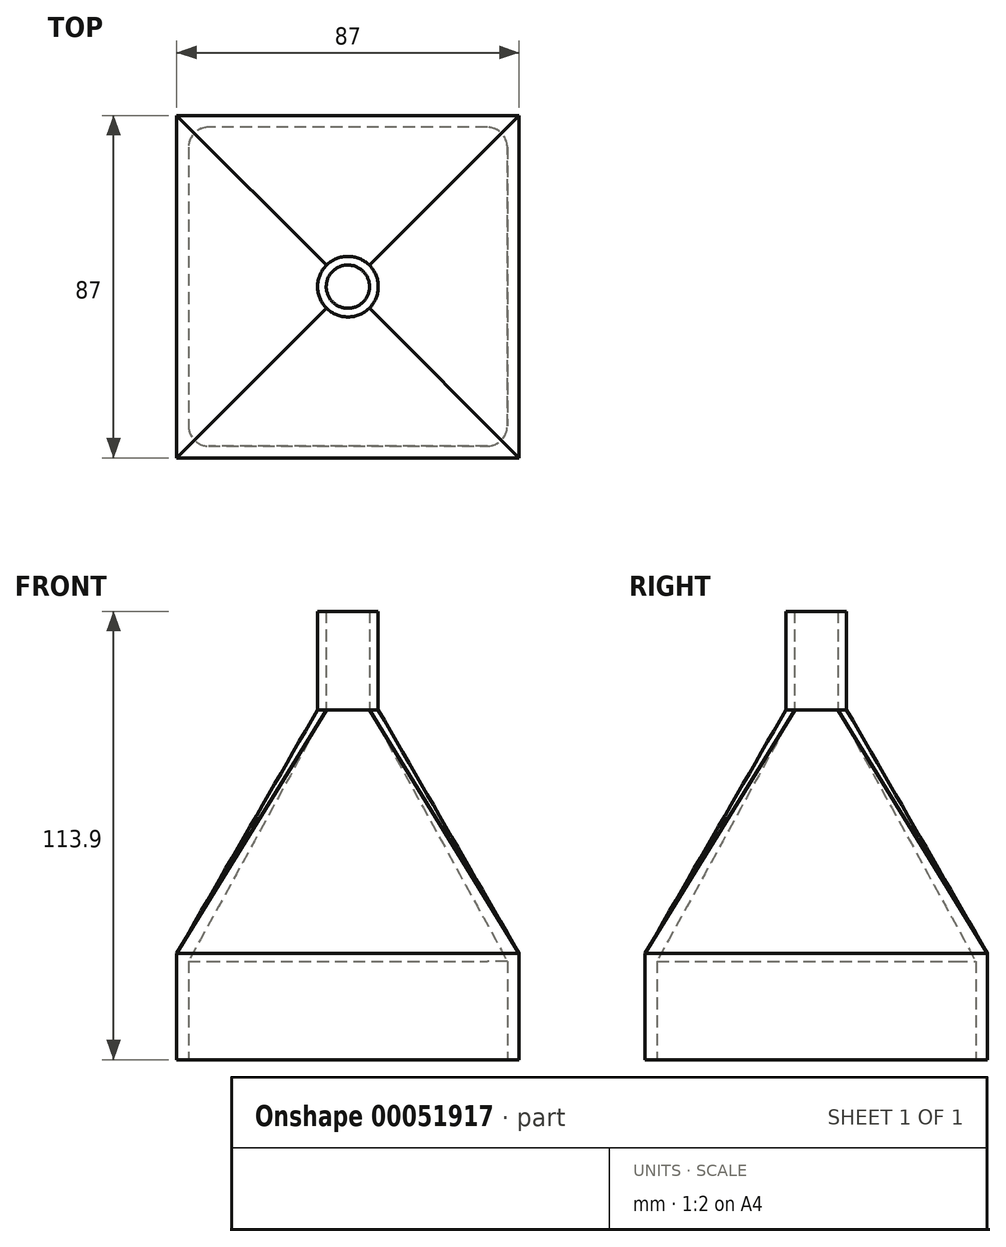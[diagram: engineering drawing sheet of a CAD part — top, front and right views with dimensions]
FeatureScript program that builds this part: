
annotation { "Feature Type Name" : "Feature", "Feature Type Description" : "" }
export const myFeature = defineFeature(function(context is Context, id is Id, definition is map)
    precondition{}
    {
        {
            var Q0;
            Q0=qCreatedBy(makeId("Top.planeOp"),FACE);
            var sketch = newSketch(context, id + "F0", { "sketchPlane" : qUnion([Q0])});
            skLineSegment(sketch, "E0.rect.bottom", {"start": v(35.42, 40.5) * mm, "end": v(-35.42, 40.5) * mm});
            skLineSegment(sketch, "E0.rect.top", {"start": v(35.42, -40.5) * mm, "end": v(-35.42, -40.5) * mm});
            skLineSegment(sketch, "E0.rect.left", {"start": v(40.5, 35.42) * mm, "end": v(40.5, -35.42) * mm});
            skLineSegment(sketch, "E0.rect.right", {"start": v(-40.5, 35.42) * mm, "end": v(-40.5, -35.42) * mm});
            skPoint(sketch, "E0.rect.middle", {"position": v(0, 0) * mm});
            skPoint(sketch, "E1.visualSharp", {"position": v(-40.5, 40.5) * mm});
            skArc(sketch, "E1.filletArc", {"start": v(-35.42, 40.5) * mm, "mid": v(-39, 39) * mm, "end": v(-40.5, 35.42) * mm});
            skPoint(sketch, "E2.visualSharp", {"position": v(40.5, 40.5) * mm});
            skArc(sketch, "E2.filletArc", {"start": v(40.5, 35.42) * mm, "mid": v(39, 39) * mm, "end": v(35.42, 40.5) * mm});
            skPoint(sketch, "E3.visualSharp", {"position": v(40.5, -40.5) * mm});
            skArc(sketch, "E3.filletArc", {"start": v(35.42, -40.5) * mm, "mid": v(39, -39) * mm, "end": v(40.5, -35.42) * mm});
            skPoint(sketch, "E4.visualSharp", {"position": v(-40.5, -40.5) * mm});
            skArc(sketch, "E4.filletArc", {"start": v(-40.5, -35.42) * mm, "mid": v(-39, -39) * mm, "end": v(-35.42, -40.5) * mm});
            skLineSegment(sketch, "E5.rect.bottom", {"start": v(43.5, 43.5) * mm, "end": v(-43.5, 43.5) * mm});
            skLineSegment(sketch, "E5.rect.top", {"start": v(43.5, -43.5) * mm, "end": v(-43.5, -43.5) * mm});
            skLineSegment(sketch, "E5.rect.left", {"start": v(43.5, 43.5) * mm, "end": v(43.5, -43.5) * mm});
            skLineSegment(sketch, "E5.rect.right", {"start": v(-43.5, 43.5) * mm, "end": v(-43.5, -43.5) * mm});
            skSolve(sketch);
        }
        {
            var Q0;
            Q0=makeQuery(id+"F0.imprint","IMPRINT",FACE,{"disambiguationData":[TD([[makeQuery(id+"F0.imprint","IMPRINT",EDGE,{"derivedFrom":sQuery(id+"F0.wireOp",EDGE,"E0.rect.bottom")}),-1.0]])]});
            extrude(context, id + "F1", {"entities" : qUnion([Q0]), "depth" : 25 * mm});
        }
        {
            var Q0;
            Q0=qCreatedBy(makeId("Top.planeOp"),FACE);
            cPlane(context, id + "F2", {"entities" : qUnion([Q0]), "cplaneType" : CPlaneType.OFFSET, "offset" : 88.9 * mm, "width" : 150 * mm, "height" : 150 * mm});
        }
        {
            var Q0;
            Q0=qCreatedBy(id+"F2.planeOp",FACE);
            var sketch = newSketch(context, id + "F3", { "sketchPlane" : qUnion([Q0])});
            skCircle(sketch, "E6", {"center": v(0, 0) * mm, "radius": 7.7 * mm});
            skSolve(sketch);
        }
        {
            var Q0;
            Q0=makeQuery(id+"F1.opExtrude","CAP_FACE",FACE,{"disambiguationData":[OSD([sQuery(id+"F0.wireOp",EDGE,"E0.rect.bottom"),sQuery(id+"F0.wireOp",EDGE,"E0.rect.top"),sQuery(id+"F0.wireOp",EDGE,"E0.rect.left"),sQuery(id+"F0.wireOp",EDGE,"E0.rect.right"),sQuery(id+"F0.wireOp",EDGE,"E1.filletArc"),sQuery(id+"F0.wireOp",EDGE,"E2.filletArc"),sQuery(id+"F0.wireOp",EDGE,"E3.filletArc"),sQuery(id+"F0.wireOp",EDGE,"E4.filletArc"),sQuery(id+"F0.wireOp",EDGE,"E5.rect.bottom"),sQuery(id+"F0.wireOp",EDGE,"E5.rect.top"),sQuery(id+"F0.wireOp",EDGE,"E5.rect.left"),sQuery(id+"F0.wireOp",EDGE,"E5.rect.right")])],"isStart":false});
            var sketch = newSketch(context, id + "F4", { "sketchPlane" : qUnion([Q0])});
            skLineSegment(sketch, "E7.rect.bottom", {"start": v(43.5, 43.5) * mm, "end": v(-43.5, 43.5) * mm});
            skLineSegment(sketch, "E7.rect.top", {"start": v(43.5, -43.5) * mm, "end": v(-43.5, -43.5) * mm});
            skLineSegment(sketch, "E7.rect.left", {"start": v(43.5, 43.5) * mm, "end": v(43.5, -43.5) * mm});
            skLineSegment(sketch, "E7.rect.right", {"start": v(-43.5, 43.5) * mm, "end": v(-43.5, -43.5) * mm});
            skPoint(sketch, "E7.rect.middle", {"position": v(0, 0) * mm});
            skSolve(sketch);
        }
        {
            var Q0;
            Q0=qSketchRegion(id+"F4",true);
            extrude(context, id + "F5", {"entities" : qUnion([Q0]), "operationType" : NewBodyOperationType.ADD, "depth" : 2 * mm});
        }
        {
            var Q1;
            Q1=makeQuery(id+"F5.opExtrude","CAP_FACE",FACE,{"disambiguationData":[OSD([sQuery(id+"F4.wireOp",EDGE,"E7.rect.bottom"),sQuery(id+"F4.wireOp",EDGE,"E7.rect.top"),sQuery(id+"F4.wireOp",EDGE,"E7.rect.left"),sQuery(id+"F4.wireOp",EDGE,"E7.rect.right")])],"isStart":false});
            var Q2;
            Q2=makeQuery(id+"F3.imprint","IMPRINT",FACE,{"disambiguationData":[TD([[makeQuery(id+"F3.imprint","IMPRINT",EDGE,{"derivedFrom":sQuery(id+"F3.wireOp",EDGE,"E6")}),1.0]])]});
            loft(context, id + "F6", {"operationType" : NewBodyOperationType.ADD, "sheetProfilesArray" : [{ "sheetProfileEntities" : qUnion([Q1]) }, { "sheetProfileEntities" : qUnion([Q2]) }]});
        }
        {
            var Q0;
            Q0=makeQuery(id+"F6.opLoft","CAP_FACE",FACE,{"disambiguationData":[OSD([makeQuery(id+"F3.imprint","IMPRINT",FACE,{"disambiguationData":[TD([[makeQuery(id+"F3.imprint","IMPRINT",EDGE,{"derivedFrom":sQuery(id+"F3.wireOp",EDGE,"E6")}),1.0]])]})])],"isStart":true});
            var sketch = newSketch(context, id + "F7", { "sketchPlane" : qUnion([Q0])});
            skCircle(sketch, "E8", {"center": v(0, 0) * mm, "radius": 5.5 * mm});
            skSolve(sketch);
        }
        {
            var Q1;
            Q1=makeQuery(id+"F5.opExtrude","CAP_FACE",FACE,{"disambiguationData":[OSD([sQuery(id+"F4.wireOp",EDGE,"E7.rect.bottom"),sQuery(id+"F4.wireOp",EDGE,"E7.rect.top"),sQuery(id+"F4.wireOp",EDGE,"E7.rect.left"),sQuery(id+"F4.wireOp",EDGE,"E7.rect.right")])],"isStart":true});
            var Q2;
            Q2=makeQuery(id+"F7.imprint","IMPRINT",FACE,{"disambiguationData":[TD([[makeQuery(id+"F7.imprint","IMPRINT",EDGE,{"derivedFrom":sQuery(id+"F7.wireOp",EDGE,"E8")}),1.0]])]});
            loft(context, id + "F8", {"operationType" : NewBodyOperationType.REMOVE, "sheetProfilesArray" : [{ "sheetProfileEntities" : qUnion([Q1]) }, { "sheetProfileEntities" : qUnion([Q2]) }]});
        }
        {
            var Q0;
            Q0=makeQuery(id+"F6.opLoft","CAP_FACE",FACE,{"disambiguationData":[OSD([makeQuery(id+"F3.imprint","IMPRINT",FACE,{"disambiguationData":[TD([[makeQuery(id+"F3.imprint","IMPRINT",EDGE,{"derivedFrom":sQuery(id+"F3.wireOp",EDGE,"E6")}),1.0]])]})])],"isStart":true});
            extrude(context, id + "F9", {"entities" : qUnion([Q0]), "operationType" : NewBodyOperationType.ADD, "depth" : 25 * mm});
        }
    });
